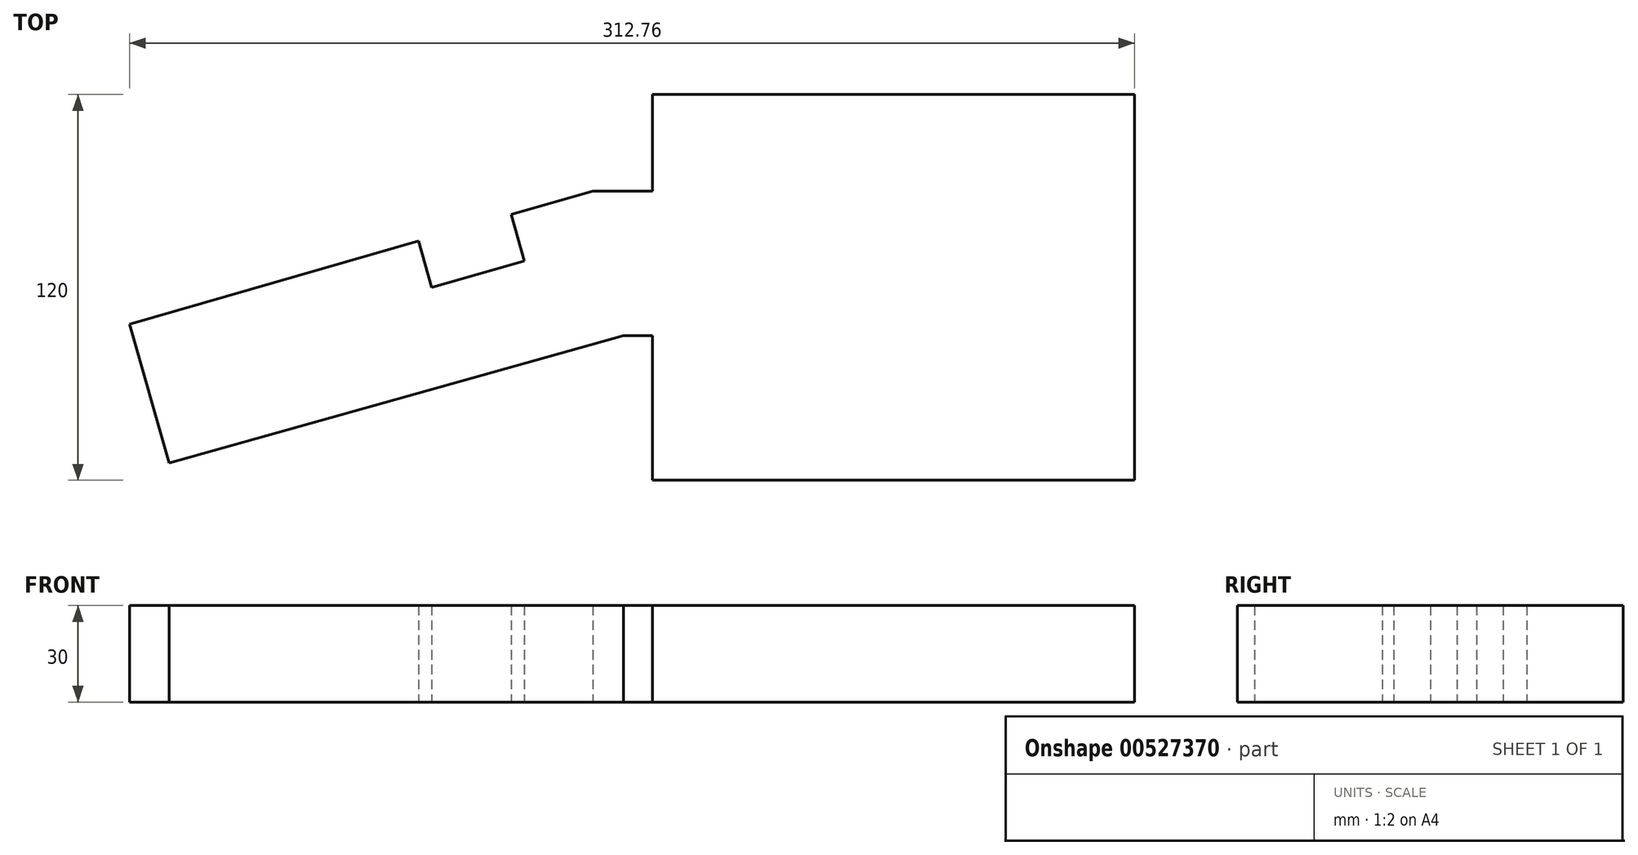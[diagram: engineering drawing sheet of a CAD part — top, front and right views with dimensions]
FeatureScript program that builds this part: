
annotation { "Feature Type Name" : "Feature", "Feature Type Description" : "" }
export const myFeature = defineFeature(function(context is Context, id is Id, definition is map)
    precondition{}
    {
        {
            var Q0;
            Q0=qCreatedBy(makeId("Top.planeOp"),FACE);
            var sketch = newSketch(context, id + "F0", { "sketchPlane" : qUnion([Q0])});
            skLineSegment(sketch, "E0.bottom", {"start": v(75, 60) * mm, "end": v(-75, 60) * mm});
            skLineSegment(sketch, "E0.top", {"start": v(75, -60) * mm, "end": v(-75, -60) * mm});
            skLineSegment(sketch, "E0.left", {"start": v(75, 60) * mm, "end": v(75, -60) * mm});
            skLineSegment(sketch, "E0.right", {"start": v(-75, 60) * mm, "end": v(-75, 30) * mm});
            skPoint(sketch, "E0.middle", {"position": v(0, 0) * mm});
            skLineSegment(sketch, "E1", {"start": v(-237.76, -11.4) * mm, "end": v(-147.85, 14.42) * mm});
            skLineSegment(sketch, "E2", {"start": v(-93.59, 30) * mm, "end": v(26.41, 30) * mm});
            skLineSegment(sketch, "E3", {"start": v(26.41, 30) * mm, "end": v(26.41, -15) * mm});
            skLineSegment(sketch, "E4", {"start": v(26.41, -15) * mm, "end": v(-84.04, -15) * mm});
            skLineSegment(sketch, "E5", {"start": v(-237.76, -11.4) * mm, "end": v(-225.34, -54.66) * mm});
            skLineSegment(sketch, "E6", {"start": v(-225.34, -54.66) * mm, "end": v(-84.04, -15) * mm});
            skLineSegment(sketch, "E7", {"start": v(-147.85, 14.42) * mm, "end": v(-143.7, 0) * mm});
            skLineSegment(sketch, "E8", {"start": v(-143.7, 0) * mm, "end": v(-114.87, 8.28) * mm});
            skLineSegment(sketch, "E9", {"start": v(-114.87, 8.28) * mm, "end": v(-119.01, 22.7) * mm});
            skLineSegment(sketch, "E10.trimOffspring", {"start": v(-119.01, 22.7) * mm, "end": v(-93.59, 30) * mm});
            skLineSegment(sketch, "E11.trimOffspring", {"start": v(-75, -15) * mm, "end": v(-75, -60) * mm});
            skSolve(sketch);
        }
        {
            var Q0;
            Q0=makeQuery(id+"F0.imprint","IMPRINT",FACE,{"disambiguationData":[TD([[makeQuery(id+"F0.imprint","IMPRINT",EDGE,{"derivedFrom":sQuery(id+"F0.wireOp",EDGE,"E0.bottom")}),1.0]])]});
            var Q1;
            Q1=makeQuery(id+"F0.imprint","IMPRINT",FACE,{"disambiguationData":[TD([[makeQuery(id+"F0.imprint","IMPRINT",EDGE,{"derivedFrom":sQuery(id+"F0.wireOp",EDGE,"E1")}),-1.0]])]});
            extrude(context, id + "F1", {"entities" : qUnion([Q0, Q1]), "depth" : 30 * mm, "offsetDistance" : 25 * mm});
        }
    });
